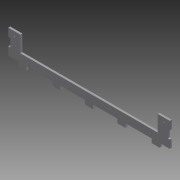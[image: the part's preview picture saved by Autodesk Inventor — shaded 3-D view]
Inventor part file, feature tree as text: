
AUTODESK INVENTOR PART (.ipt)
format: ipt  version: 2011 (Build 150239000, 239)  size: 741,888 bytes
history: native  units: in
note: dims shown in document units (in); Inventor stores cm internally (conversion verified against a paired STEP export)
features: extrude x26, sketch x26, fillet x2
ambient origin geometry x8: Origin, YZ Plane, XZ Plane, XY Plane, X Axis, Y Axis, Z Axis, Center Point
bodies: Solid1 (feature_tree)
feature tree (54):
  extrude  "Extrusion1"  Depth=41.5in
  extrude  "Extrusion2"  Depth=10.0in
  extrude  "Extrusion3"  Depth=0.6in
  extrude  "Extrusion4"  Depth=0.25in
  extrude  "Extrusion5"  Depth=0.5in
  extrude  "Extrusion6"  Depth=1.0in
  extrude  "Extrusion7"  Depth=4.1in TaperAngle=0.0deg
  extrude  "Extrusion8"  Depth=1.0in
  extrude  "Extrusion9"  Depth=1.0in
  extrude  "Extrusion10"  Depth=1.0in
  extrude  "Extrusion11"  Depth=4.1in TaperAngle=0.0deg
  extrude  "Extrusion12"  Depth=0.5in
  fillet  "Fillet1"  Radius=0.25in
  fillet  "Fillet2"  Radius=1.0in
  extrude  "Extrusion13"  Depth=3.0in
  extrude  "Extrusion14"  Depth=3.0in
  extrude  "Extrusion15"  Depth=3.0in
  extrude  "Extrusion16"  Depth=3.0in
  extrude  "Extrusion17"  Depth=3.0in
  extrude  "Extrusion18"  Depth=0.25in
  extrude  "Extrusion19"  Depth=0.25in TaperAngle=0.0deg
  extrude  "Extrusion20"  Depth=0.25in
  extrude  "Extrusion21"  Depth=1.0in
  extrude  "Extrusion22"  Depth=1.0in
  extrude  "Extrusion23"  Depth=0.156in
  extrude  "Extrusion24"  Depth=0.156in
  extrude  "Extrusion25"  Depth=0.25in TaperAngle=0.0deg
  extrude  "Extrusion26"  Depth=0.25in TaperAngle=0.0deg
  sketch  "Sketch1"  dims[d0=20.0in d1=41.5in]
  sketch  "Sketch2"  dims[d2=0.25in d3=0.0in d4=10.0in]
  sketch  "Sketch3"  dims[d5=0.25in d6=0.6in]
  sketch  "Sketch4"  dims[d7=1.2in d8=0.25in]
  sketch  "Sketch5"  dims[d9=4.1in d10=0.0in d11=0.5in]
  sketch  "Sketch6"  dims[d12=0.5in d13=1.0in]
  sketch  "Sketch7"  dims[d14=1.0in d15=4.1in d16=0.0in]
  sketch  "Sketch8"  dims[d17=1.0in d18=1.0in]
  sketch  "Sketch9"  dims[d19=1.0in d20=1.0in]
  sketch  "Sketch10"  dims[d21=6.75in d22=1.0in]
  sketch  "Sketch11"  dims[d23=0.5in d24=4.1in d25=0.0in]
  sketch  "Sketch12"  dims[d26=0.25in d27=0.5in d28=0.25in d29=0.0in d30=1.0in]
  sketch  "Sketch13"  dims[d31=1.0in d32=3.0in]
  sketch  "Sketch14"  dims[d33=1.0in d34=3.0in]
  sketch  "Sketch15"  dims[d35=1.0in d36=3.0in]
  sketch  "Sketch16"  dims[d37=1.0in d38=3.0in]
  sketch  "Sketch17"  dims[d39=1.0in d40=3.0in]
  sketch  "Sketch18"  dims[d41=1.0in d42=0.25in]
  sketch  "Sketch19"  dims[d43=1.0in d44=0.0in d45=0.25in d46=0.0in]
  sketch  "Sketch20"  dims[d47=1.0in d48=0.25in]
  sketch  "Sketch21"  dims[d49=1.0in d50=1.0in]
  sketch  "Sketch22"  dims[d51=1.0in d52=1.0in]
  sketch  "Sketch23"  dims[d53=0.25in d54=0.0in d55=0.156in]
  sketch  "Sketch24"  dims[d56=0.156in d57=0.156in]
  sketch  "Sketch25"  dims[d58=0.156in d59=0.25in d60=0.0in]
  sketch  "Sketch26"  dims[d61=0.25in d62=0.0in d63=0.25in d64=0.0in d65=1.0in d66=1.0in d67=1.0in d68=1.0in d69=1.0in d70=1.0in d71=1.0in d72=1.0in d73=0.25in d74=0.0in d75=0.5in d76=0.5in d77=1.0in d78=0.0in d79=3.0in d80=3.0in d81=0.25in d82=0.0in d83=0.75in d84=0.75in d85=0.75in d86=0.75in d87=0.156in d88=0.156in d89=0.25in d90=0.0in d91=0.25in d92=1.0in d93=1.0in d94=1.0in d95=0.25in d96=0.0in d97=0.25in d98=1.0in d99=1.0in d100=1.0in d101=0.25in d102=0.0in d103=1.0in d104=0.0in d105=0.75in d106=0.5in d107=0.156in d108=0.156in d109=1.0in d110=0.0in d111=0.25in d112=0.0in d113=0.5in d114=0.5in d115=1.0in d116=0.25in d117=1.0in d118=1.0in d119=1.0in d120=1.0in d121=1.0in d122=1.0in d123=1.0in d124=1.0in d125=1.0in d126=1.0in d127=1.0in d128=1.0in d129=1.0in d130=1.0in d131=1.0in d132=1.0in d133=1.0in d134=1.0in d135=0.25in d136=0.0in d137=0.25in d138=0.0in d139=1.0in d140=0.0in d141=1.25in d142=1.0in d143=0.25in d144=1.0in d145=0.25in d146=1.0in d147=3.25in d148=1.0in d149=3.0in d150=1.0in d151=1.0in d152=2.0in d153=1.0in d154=0.25in d155=0.0in d156=0.25in d157=0.25in d158=0.0in d159=0.25in d160=0.0in]
